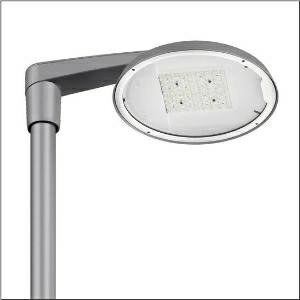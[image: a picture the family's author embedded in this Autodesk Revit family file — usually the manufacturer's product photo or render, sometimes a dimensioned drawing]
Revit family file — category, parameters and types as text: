
# Revit family: dl_50_iq_mini___st0_5a_5xa248b41f08me_9f99
name_source: partatom
category: Lighting Fixtures
units: mm (PartAtom-declared; Revit-internal decimal feet)

## family parameters
Cut with Voids When Loaded = No
Host = Face
Light Source = No
Part Type = Normal
Room Calculation Point = No
Round Connector Dimension = Use Diameter
Shared = No

## types (1)
- --- (1 x LED, 15660 lm, 101.7 W, 4000K)
    Apparent Load = 102 VA
    CIE Flux Codes = 41 75 97 100 100
    Color Rendering = 70
    Color Temperature = 4000K
    Default Elevation = 1800 mm
    Description = DL 50 iQ mini, mast luminaire, primary light control with lens, of PMMA, primary optical cover: cover, of toughened safety glass, transparent, light distribution: ST0.5a, light emission: direct distribution, primary light characteristic: asymmetric, installation type: side-entry, post-top, LED, High Power LED, rated luminous flux: 15.660lm, luminous efficacy: 154lm/W, light colour: 740, colour temperature: 4000K, control gear: iQ Street-Remote, control: optimised constant luminous flux control (CLO 2.0), Desk-Remote (wireless, voltage-free reading and setting of iQ features in the workshop via application-optimized NFC function/RFID function), Light-Fading, Smart-Wire, Night-Set, Lumen-Switch, Temp-Guard, Auto-Match, Street-Remote, mains connection: 230..240V, AC, 50/60Hz, connection cable pre-assembled, cable length: 10,5m, start of lifetime: 102W, end of service life: 111W, reduction: 45W, luminaire housing, of diecast aluminium, powder-coated, SITECO metallic grey (DB 702S), inclination adjustable: 0°, 5°, 10° (post-top) | 0°, -5°, -10°, -15° (side-entry), please order mast post-top element or mast side-entry element separately, diameter: 500mm, height: 115mm, post-top: for spigot size d x l = 76 x 100mm; with reducer (optional accessory) 60 x 100mm | side-entry: for spigot size d x l = 60 x 100mm; with reducer (optional accessory) 42 x 100mm, mounting height: 4..6m, protection rating (complete): IP66, insulation class (complete): insulation class II (safety insulation), certification: CE, ENEC, ENEC+, VDE, impact resistance: IK08, permissible operating ambient temperature for outdoor applications: -25..+40°C, standard-compliant lighting for roads and squares, packaging unit: 1 piece

Light Distribution: ST0.5a
    Height = 115 mm
    Lamp = 1 x LED
    Lamp Light Flux = 15660 lm
    Lamp Power = 101.7 W
    Lamp count = 1
    Length = 500 mm
    Luminous efficacy = 154 lm/W
    Manufacturer = Siteco
    ModVariant = No
    Model = 5XA248B41F08ME
    Number of Poles = 1
    OnlyDefault = Yes
    Power Factor = 1
    Product Name = DL 50 iQ mini | ST0.5a
    Product group = mast luminaire | pylon top
    ProductGroupID = 6100
    Protection Class = Protection class II
    Protection Degree = IP 66
    RLX_Detail_Level = 1
    RLX_Emergency_Light_Flux = 0 lm
    RLX_Emergency_Type = 0
    RLX_Emergency_Type_DB = No
    RlxData = <blob elided: 127521 chars, md5=e15f4ac2>
    Socket = socket
    Standby Power = 0 W
    System Light Flux = 15660 lm
    System Power = 102 W
    Type Comments = factory setting: luminous flux: 100 % | dim-lin: 254 | 534 mA
    Type Image = l_1251790.jpg
    URL = http://relux.com
    VarID = @adj_142529
    Voltage = 0 V
    Weight = 0.00 kg
    Width = 0 mm  [stored 0 ft]

note: [stored X ft] marks values corroborated as IEEE doubles in the binary element streams (Revit-internal decimal feet)

## geometry (parser evidence)
native form markers: Blend x4, Sweep x11
no freeform markers — native parametric forms only
